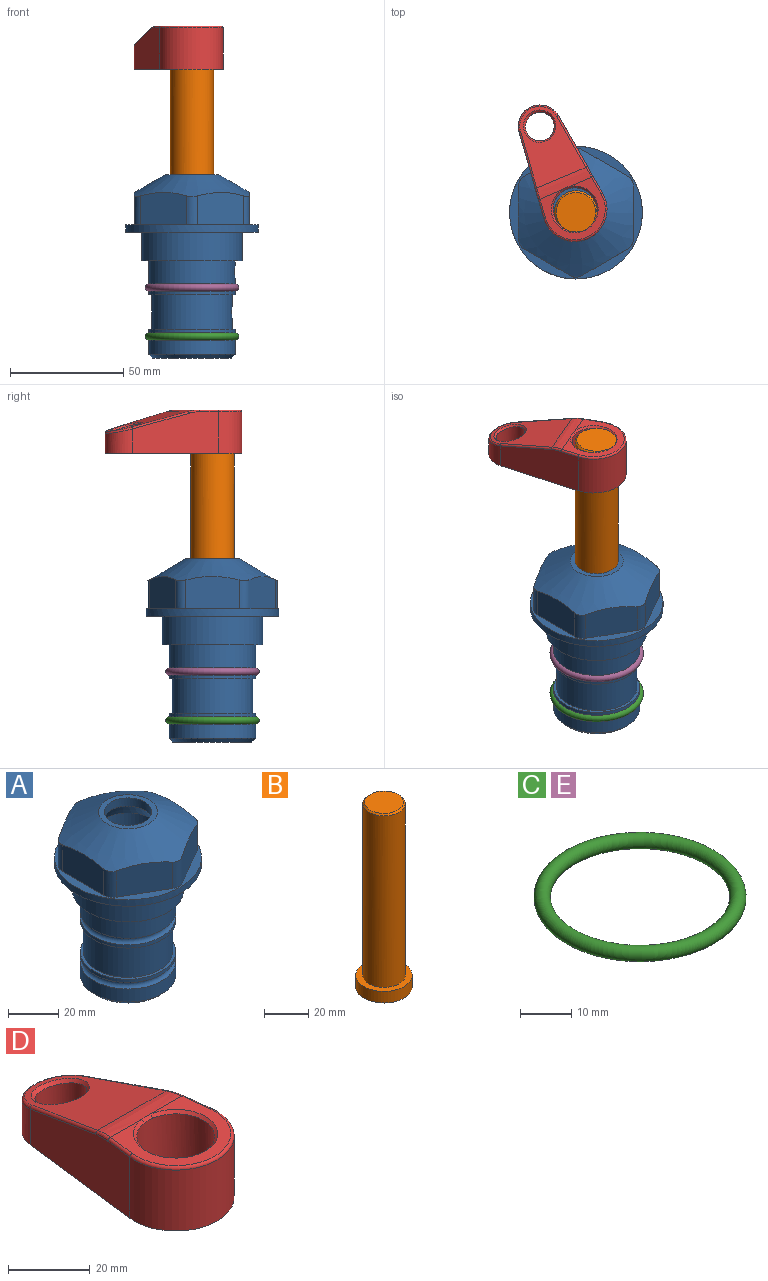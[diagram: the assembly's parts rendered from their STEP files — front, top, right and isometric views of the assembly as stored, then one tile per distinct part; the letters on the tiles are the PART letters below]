
ASSEMBLY  parts=5 mates=4
PART A: 36 faces, bbox 58.7x58.7x81 mm
  f0: cylinder r=17.78mm len=35.56mm, axis (0,0,1), area 1670.8mm2, adj f23,f24,f31
  f1: cylinder r=19.05mm len=38.1mm, axis (0,0,1), area 1191.9mm2, adj f26,f27,f30
  f2: plane 58.66x58.66mm, normal (0,0,-1), area 1150.6mm2, adj f3,f28
  f3: cylinder r=29.33mm len=58.66mm, axis (0,0,-1), area 585.1mm2, adj f2,f4
  f4: plane 58.66x58.66mm, normal (0,0,1), area 475.9mm2, adj f3,f5,f6,f7,f8,f9,f10,f11
  f5: plane 20.32x14.34mm, normal (-0.5,0.87,0), area 324.4mm2, adj f4,f15,f16,f17
  f6: plane 20.32x14.34mm, normal (0.5,0.87,0), area 324.4mm2, adj f4,f14,f15,f17
  f7: plane 23.48x14.34mm, normal (1,0,0), area 324.4mm2, adj f4,f13,f14,f17
  f8: plane 20.32x14.34mm, normal (0.5,-0.87,0), area 324.4mm2, adj f4,f12,f13,f17
  f9: plane 20.32x14.34mm, normal (-0.5,-0.87,0), area 324.4mm2, adj f4,f11,f12,f17
  f10: plane 23.48x14.34mm, normal (-1,0,0), area 324.4mm2, adj f4,f11,f16,f17
  f11: cylinder r=5.08mm len=12.85mm, axis (0,0,-1), area 67.2mm2, adj f4,f9,f10,f17
  f12: cylinder r=5.08mm len=12.85mm, axis (0,0,-1), area 67.2mm2, adj f4,f8,f9,f17
  f13: cylinder r=5.08mm len=12.85mm, axis (0,0,-1), area 67.2mm2, adj f4,f7,f8,f17
  f14: cylinder r=5.08mm len=12.85mm, axis (0,0,-1), area 67.2mm2, adj f4,f6,f7,f17
  f15: cylinder r=5.08mm len=12.85mm, axis (0,0,-1), area 67.2mm2, adj f4,f5,f6,f17
  f16: cylinder r=5.08mm len=12.85mm, axis (0,0,-1), area 67.2mm2, adj f4,f5,f10,f17
  f17: cone r=11.73mm half-angle=60deg, axis (0,0,-1), area 2071.8mm2, adj f5,f6,f7,f8,f9,f10,f11,f12
  f18: plane 23.46x23.46mm, normal (0,0,1), area 147.4mm2, adj f17,f35
  f19: plane 34.93x34.93mm, normal (0,0,-1), area 958mm2, adj f29
  f20: cylinder r=19.05mm len=38.1mm, axis (0,0,1), area 760.1mm2, adj f21,f29
  f21: torus R=19.05mm, axis (0,0,1), area 565.3mm2, adj f20,f22
  f22: cylinder r=19.05mm len=38.1mm, axis (0,0,1), area 190mm2, adj f21,f23
  f23: plane 38.1x38.1mm, normal (0,0,1), area 146.9mm2, adj f0,f22
  f24: plane 38.1x38.1mm, normal (0,0,-1), area 146.9mm2, adj f0,f25
  f25: cylinder r=19.05mm len=38.1mm, axis (0,0,1), area 190mm2, adj f24,f26
  f26: torus R=19.05mm, axis (0,0,1), area 565.3mm2, adj f1,f25
  f27: plane 44.45x44.45mm, normal (0,0,-1), area 411.7mm2, adj f1,f28
  f28: cylinder r=22.23mm len=44.45mm, axis (0,0,1), area 1773.5mm2, adj f2,f27
  f29: cone r=19.05mm half-angle=45deg, axis (0,0,1), area 257.5mm2, adj f19,f20
  f30: cylinder r=3.17mm len=6.75mm, axis (-1,0,0), area 128mm2, adj f1,f33
  f31: cylinder r=3.17mm len=6.35mm, axis (-1,0,0), area 102.5mm2, adj f0,f33
  f32: plane 25.4x25.4mm, normal (0,0,1), area 506.7mm2, adj f33
  f33: cylinder r=12.7mm len=66.42mm, axis (0,0,-1), area 5236.2mm2, adj f30,f31,f32,f34
  f34: cone r=9.53mm half-angle=30deg, axis (0,0,-1), area 443.4mm2, adj f33,f35
  f35: cylinder r=9.53mm len=19.05mm, axis (0,0,-1), area 240.9mm2, adj f18,f34
PART B: 6 faces, bbox 25.4x25.4x101.6 mm
  f0: plane 17.46x17.46mm, normal (0,0,1), area 239.5mm2, adj f5
  f1: plane 25.4x25.4mm, normal (0,0,-1), area 506.7mm2, adj f2
  f2: cylinder r=12.7mm len=25.4mm, axis (0,0,1), area 506.7mm2, adj f1,f3
  f3: plane 25.4x25.4mm, normal (0,0,1), area 221.7mm2, adj f2,f4
  f4: cylinder r=9.53mm len=94.46mm, axis (0,0,1), area 5653mm2, adj f3,f5
  f5: cone r=8.73mm half-angle=45deg, axis (0,0,-1), area 64.4mm2, adj f0,f4
PART C: 1 faces, bbox 44.7x44.7x3.2 mm
  f0: torus R=19.05mm, axis (0,0,1), area 1193.9mm2
PART D: 31 faces, bbox 31.7x65.5x19.8 mm
  f0: plane 39.12x18.26mm, normal (0.99,0.12,0), area 612.2mm2, adj f1,f4,f7,f11,f13,f15
  f1: cylinder r=9.53mm len=18.91mm, axis (0,0,-1), area 296.1mm2, adj f0,f2,f7,f17
  f2: plane 39.12x18.26mm, normal (-0.99,0.12,0), area 612.2mm2, adj f1,f4,f7,f12,f14,f16
  f3: cylinder r=6.35mm len=12.7mm, axis (0,0,-1), area 362.4mm2, adj f7,f18
  f4: cylinder r=14.29mm len=28.58mm, axis (0,0,-1), area 882.2mm2, adj f0,f2,f7,f10
  f5: cylinder r=9.53mm len=19.05mm, axis (0,0,-1), area 1092.6mm2, adj f7,f19,f20
  f6: plane 26.99x23.69mm, normal (0,0,1), area 216.2mm2, adj f9,f10,f11,f12,f19
  f7: plane 63.5x28.58mm, normal (0,0,-1), area 661.8mm2, adj f0,f1,f2,f3,f4,f5,f22,f23
  f8: plane 33.52x23.6mm, normal (0,0.26,0.97), area 486mm2, adj f9,f15,f16,f17,f18
  f9: cylinder r=19.05mm len=24.72mm, axis (1,0,0), area 120.4mm2, adj f6,f8,f13,f14,f20
  f10: torus R=13.49mm, axis (0,0,1), area 59mm2, adj f4,f6,f11,f12
  f11: cylinder r=0.79mm len=8.67mm, axis (0.12,-0.99,0), area 10.8mm2, adj f0,f6,f10,f13
  f12: cylinder r=0.79mm len=8.67mm, axis (0.12,0.99,0), area 10.8mm2, adj f2,f6,f10,f14
  f13: bspline ~4.95x1.42mm, area 6.1mm2, adj f0,f9,f11,f15
  f14: bspline ~4.95x1.42mm, area 6.1mm2, adj f2,f9,f12,f16
  f15: cylinder r=0.79mm len=25.95mm, axis (0.12,-0.96,0.26), area 32.9mm2, adj f0,f8,f13,f17
  f16: cylinder r=0.79mm len=25.95mm, axis (0.12,0.96,-0.26), area 32.9mm2, adj f2,f8,f14,f17
  f17: bspline ~18.91x8.38mm, area 30mm2, adj f1,f8,f15,f16
  f18: bspline ~14.29x14.29mm, area 48.3mm2, adj f3,f8
  f19: cone r=9.53mm half-angle=45deg, axis (0,0,1), area 66.5mm2, adj f5,f6,f20
  f20: bspline ~3.22x0.96mm, area 3.5mm2, adj f5,f9,f19
  f21: plane 2.75x2.72mm, normal (0,0,-1), area 2.9mm2, adj f23,f25,f28
  f22: plane 23.05x15.88mm, normal (-0.99,-0.12,0), area 323.6mm2, adj f7,f25,f26,f27,f28,f29
  f23: plane 23.05x15.88mm, normal (0.99,-0.12,0), area 323.6mm2, adj f7,f21,f25,f27,f28,f30
  f24: cylinder r=9.53mm len=10.69mm, axis (0,0,-1), area 114.7mm2, adj f7,f27,f29,f30
  f25: cylinder r=12.7mm len=20.59mm, axis (0,0,-1), area 381.1mm2, adj f7,f21,f22,f23,f26,f28
  f26: plane 2.75x2.72mm, normal (0,0,-1), area 2.9mm2, adj f22,f25,f28
  f27: plane 19.72x18.37mm, normal (0,-0.26,-0.97), area 291.8mm2, adj f22,f23,f24,f28,f29,f30
  f28: cylinder r=15.88mm len=19.92mm, axis (1,0,0), area 54.8mm2, adj f21,f22,f23,f25,f26,f27
  f29: cylinder r=1.59mm len=11mm, axis (0,0,-1), area 34.7mm2, adj f7,f22,f24,f27
  f30: cylinder r=1.59mm len=11mm, axis (0,0,-1), area 34.7mm2, adj f7,f23,f24,f27
PART E: same geometry as C
PLACE A at identity fixed
PLACE B rot(axis=(0,0,1),22.9deg) t=(0,0,27.55)mm
PLACE C t=(0,0,-21.59)mm
PLACE D rot(axis=(0,0,1),22.9deg) t=(-0.55,1.32,27.55)mm
PLACE E at identity
MATE fastened D.f6 <-> B.f2  axis (0,0,1) through (0,0,91.05)mm
MATE cylindrical B.f2 <-> A.f0  axis (0,0,-1) through (0,0,-10.55)mm
MATE fastened A.f0 <-> C.f0  axis (0,0,1) through (0,0,-46.1)mm
MATE fastened A.f0 <-> E.f0  axis (0,0,1) through (0,0,-24.51)mm
